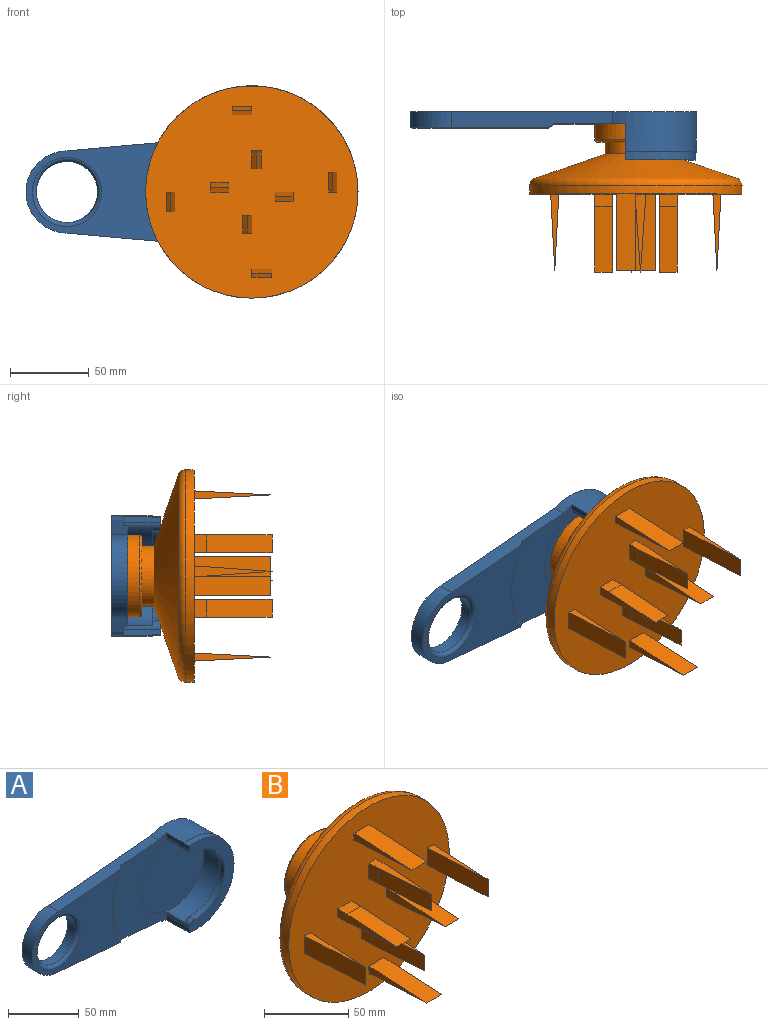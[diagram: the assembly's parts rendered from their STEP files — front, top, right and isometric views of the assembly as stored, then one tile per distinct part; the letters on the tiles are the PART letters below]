
ASSEMBLY  parts=2 mates=1
PART A: 21 faces, bbox 181.3x30.5x76.4 mm
  f0: cylinder r=38.19mm len=76.39mm, axis (0,1,0), area 3516.6mm2, adj f5,f6,f9,f10,f11,f14,f16
  f1: plane 63.76x63.76mm, normal (0,-1,0), area 3193.1mm2, adj f2
  f2: cylinder r=31.88mm len=63.76mm, axis (0,-1,0), area 2253mm2, adj f1,f3,f9,f12,f13
  f3: plane 63.76x37.97mm, normal (0,1,0), area 338.2mm2, adj f2,f4,f12,f13
  f4: cylinder r=28.64mm len=57.29mm, axis (0,-1,0), area 471mm2, adj f3,f7,f12,f13
  f5: plane 76.39x44.88mm, normal (0,-1,0), area 45.9mm2, adj f0,f8,f10,f11
  f6: plane 181.28x76.39mm, normal (0,1,0), area 9548.2mm2, adj f0,f14,f15,f16,f19
  f7: plane 75.7x44.53mm, normal (0,-1,0), area 1071mm2, adj f4,f8,f10,f11,f12,f13
  f8: cylinder r=37.85mm len=75.7mm, axis (0,1,0), area 672.3mm2, adj f5,f7,f10,f11
  f9: plane 75.21x54.97mm, normal (0,-1,0), area 2310.9mm2, adj f0,f2,f10,f11,f12,f13,f14,f16
  f10: plane 22.86x3.92mm, normal (-1,0,0), area 87.8mm2, adj f0,f5,f7,f8,f9,f12
  f11: plane 22.86x3.92mm, normal (-1,0,0), area 87.8mm2, adj f0,f5,f7,f8,f9,f13
  f12: cylinder r=5.08mm len=22.86mm, axis (0,-1,0), area 86mm2, adj f2,f3,f4,f7,f9,f10
  f13: cylinder r=5.08mm len=22.86mm, axis (0,-1,0), area 86mm2, adj f2,f3,f4,f7,f9,f11
  f14: plane 102.33x10.16mm, normal (-0.09,0,1), area 944.6mm2, adj f0,f6,f9,f15,f17,f18
  f15: cylinder r=26.06mm len=52.12mm, axis (0,1,0), area 831.7mm2, adj f6,f14,f16,f17
  f16: plane 102.33x10.16mm, normal (-0.09,0,-1), area 944.6mm2, adj f0,f6,f9,f15,f17,f18
  f17: plane 87.91x63.23mm, normal (0,-1,0), area 2767mm2, adj f14,f15,f16,f18,f20
  f18: cone r=38.19mm half-angle=45deg, axis (0,-1,0), area 239.4mm2, adj f9,f14,f16,f17
  f19: cylinder r=19.36mm len=38.73mm, axis (0,1,0), area 927.1mm2, adj f6,f20
  f20: torus R=21.9mm, axis (0,-1,0), area 508.6mm2, adj f17,f19
PART B: 50 faces, bbox 145.6x95.1x145.6 mm
  f0: plane 134.54x134.54mm, normal (0,-1,0), area 13696.1mm2, adj f1,f7,f8,f9,f10,f11,f12,f13
  f1: cylinder r=67.27mm len=134.54mm, axis (0,-1,0), area 2226mm2, adj f0,f47
  f2: cone r=67.27mm half-angle=71deg, axis (0,-1,0), area 12303.2mm2, adj f3,f47
  f3: cylinder r=19.32mm len=38.65mm, axis (0,-1,0), area 925.1mm2, adj f2,f6
  f4: cylinder r=25.97mm len=51.95mm, axis (0,-1,0), area 1658.1mm2, adj f48,f49
  f5: plane 49.41x49.41mm, normal (0,1,0), area 1917.2mm2, adj f49
  f6: plane 49.41x49.41mm, normal (0,-1,0), area 744.2mm2, adj f3,f48
  f7: plane 48.49x5.08mm, normal (-1,0,0), area 123.2mm2, adj f0,f31,f32
  f8: plane 48.49x5.08mm, normal (1,0,0), area 123.2mm2, adj f0,f31,f32
  f9: plane 49.41x5.84mm, normal (0,0,1), area 166.6mm2, adj f0,f10,f12,f33,f34
  f10: plane 11.37x7.62mm, normal (-1,0,0), area 86.7mm2, adj f0,f9,f11,f34
  f11: plane 49.41x5.84mm, normal (0,0,-1), area 166.6mm2, adj f0,f10,f12,f33,f34
  f12: plane 11.37x7.62mm, normal (1,0,0), area 86.7mm2, adj f0,f9,f11,f33
  f13: plane 48.49x5.08mm, normal (0,0,1), area 123.2mm2, adj f0,f41,f42
  f14: plane 48.49x5.08mm, normal (0,0,-1), area 123.2mm2, adj f0,f41,f42
  f15: plane 49.41x5.84mm, normal (1,0,0), area 166.6mm2, adj f0,f16,f18,f35,f36
  f16: plane 11.37x7.62mm, normal (0,0,1), area 86.7mm2, adj f0,f15,f17,f36
  f17: plane 49.41x5.84mm, normal (-1,0,0), area 166.6mm2, adj f0,f16,f18,f35,f36
  f18: plane 11.37x7.62mm, normal (0,0,-1), area 86.7mm2, adj f0,f15,f17,f35
  f19: plane 48.49x5.08mm, normal (-1,0,0), area 123.2mm2, adj f0,f43,f44
  f20: plane 48.49x5.08mm, normal (1,0,0), area 123.2mm2, adj f0,f43,f44
  f21: plane 49.41x5.84mm, normal (0,0,1), area 166.6mm2, adj f0,f22,f24,f37,f38
  f22: plane 11.37x7.62mm, normal (-1,0,0), area 86.7mm2, adj f0,f21,f23,f37
  f23: plane 49.41x5.84mm, normal (0,0,-1), area 166.6mm2, adj f0,f22,f24,f37,f38
  f24: plane 11.37x7.62mm, normal (1,0,0), area 86.7mm2, adj f0,f21,f23,f38
  f25: plane 48.49x5.08mm, normal (0,0,-1), area 123.2mm2, adj f0,f45,f46
  f26: plane 48.49x5.08mm, normal (0,0,1), area 123.2mm2, adj f0,f45,f46
  f27: plane 49.41x5.84mm, normal (-1,0,0), area 166.6mm2, adj f0,f28,f30,f39,f40
  f28: plane 11.37x7.62mm, normal (0,0,-1), area 86.7mm2, adj f0,f27,f29,f39
  f29: plane 49.41x5.84mm, normal (1,0,0), area 166.6mm2, adj f0,f28,f30,f39,f40
  f30: plane 11.37x7.62mm, normal (0,0,1), area 86.7mm2, adj f0,f27,f29,f40
  f31: plane 48.49x12.55mm, normal (0,-0.05,1), area 609.3mm2, adj f0,f7,f8,f32
  f32: plane 48.49x12.55mm, normal (0,-0.05,-1), area 609.3mm2, adj f0,f7,f8,f31
  f33: plane 41.79x11.37mm, normal (1,-0.07,0), area 476.5mm2, adj f9,f11,f12,f34
  f34: plane 41.79x11.37mm, normal (-1,-0.07,0), area 476.5mm2, adj f9,f10,f11,f33
  f35: plane 41.79x11.37mm, normal (0,-0.07,-1), area 476.5mm2, adj f15,f17,f18,f36
  f36: plane 41.79x11.37mm, normal (0,-0.07,1), area 476.5mm2, adj f15,f16,f17,f35
  f37: plane 41.79x11.37mm, normal (-1,-0.07,0), area 476.5mm2, adj f21,f22,f23,f38
  f38: plane 41.79x11.37mm, normal (1,-0.07,0), area 476.5mm2, adj f21,f23,f24,f37
  f39: plane 41.79x11.37mm, normal (0,-0.07,-1), area 476.5mm2, adj f27,f28,f29,f40
  f40: plane 41.79x11.37mm, normal (0,-0.07,1), area 476.5mm2, adj f27,f29,f30,f39
  f41: plane 48.49x12.55mm, normal (1,-0.05,0), area 609.3mm2, adj f0,f13,f14,f42
  f42: plane 48.49x12.55mm, normal (-1,-0.05,0), area 609.3mm2, adj f0,f13,f14,f41
  f43: plane 48.49x12.55mm, normal (0,-0.05,-1), area 609.3mm2, adj f0,f19,f20,f44
  f44: plane 48.49x12.55mm, normal (0,-0.05,1), area 609.3mm2, adj f0,f19,f20,f43
  f45: plane 48.49x12.55mm, normal (1,-0.05,0), area 609.3mm2, adj f0,f25,f26,f46
  f46: plane 48.49x12.55mm, normal (-1,-0.05,0), area 609.3mm2, adj f0,f25,f26,f45
  f47: torus R=62.19mm, axis (0,1,0), area 2613.2mm2, adj f1,f2
  f48: torus R=24.7mm, axis (0,1,0), area 319.8mm2, adj f4,f6
  f49: torus R=24.7mm, axis (0,1,0), area 319.8mm2, adj f4,f5
PLACE A t=(-68.68,61.27,121.5)mm
PLACE B t=(-68.68,9.2,121.5)mm
MATE revolute B.f4 <-> A.f2  axis (0,1,0) through (-68.68,54.92,121.5)mm
